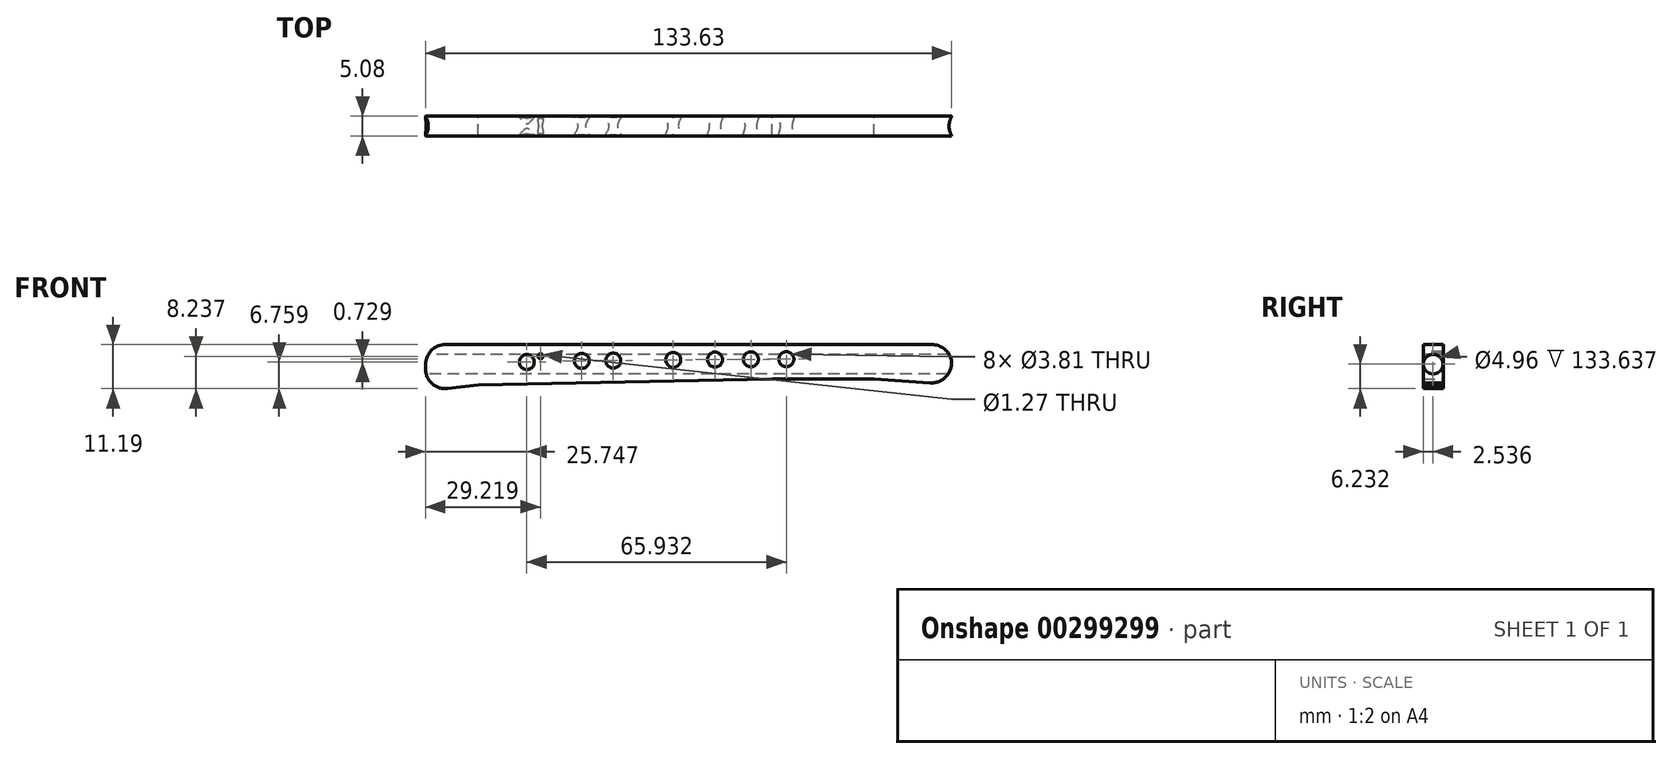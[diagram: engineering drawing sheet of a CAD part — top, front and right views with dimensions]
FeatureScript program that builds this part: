
annotation { "Feature Type Name" : "Feature", "Feature Type Description" : "" }
export const myFeature = defineFeature(function(context is Context, id is Id, definition is map)
    precondition{}
    {
        {
            var Q0;
            Q0=qCreatedBy(makeId("Front.planeOp"),FACE);
            var sketch = newSketch(context, id + "F0", { "sketchPlane" : qUnion([Q0])});
            skLineSegment(sketch, "E0", {"start": v(-67.8, 14.78) * mm, "end": v(-67.8, 2.96) * mm});
            skLineSegment(sketch, "E1", {"start": v(-67.8, 14.78) * mm, "end": v(64.84, 14.78) * mm});
            skLineSegment(sketch, "E2", {"start": v(-67.8, 2.96) * mm, "end": v(-54.4, 4.53) * mm});
            skLineSegment(sketch, "E3", {"start": v(-54.4, 4.53) * mm, "end": v(20.3, 6.1) * mm});
            skLineSegment(sketch, "E4", {"start": v(20.3, 6.1) * mm, "end": v(46.11, 6.1) * mm});
            skLineSegment(sketch, "E5", {"start": v(46.11, 6.1) * mm, "end": v(67.4, 4.53) * mm});
            skLineSegment(sketch, "E6", {"start": v(64.84, 14.78) * mm, "end": v(67.4, 4.53) * mm});
            skSolve(sketch);
        }
        {
            var Q0;
            Q0=makeQuery(id+"F0.imprint","IMPRINT",FACE,{"disambiguationData":[TD([[makeQuery(id+"F0.imprint","IMPRINT",EDGE,{"derivedFrom":sQuery(id+"F0.wireOp",EDGE,"E0")}),1.0]])]});
            extrude(context, id + "F1", {"entities" : qUnion([Q0]), "depth" : 5.08 * mm});
        }
        {
            var Q0;
            Q0=makeQuery(id+"F1.opExtrude","CAP_FACE",FACE,{"disambiguationData":[OSD([sQuery(id+"F0.wireOp",EDGE,"E0"),sQuery(id+"F0.wireOp",EDGE,"E1"),sQuery(id+"F0.wireOp",EDGE,"E2"),sQuery(id+"F0.wireOp",EDGE,"E3"),sQuery(id+"F0.wireOp",EDGE,"E4"),sQuery(id+"F0.wireOp",EDGE,"E5"),sQuery(id+"F0.wireOp",EDGE,"E6")])],"isStart":false});
            var sketch = newSketch(context, id + "F2", { "sketchPlane" : qUnion([Q0])});
            skCircle(sketch, "E7", {"center": v(-42.04, 10.35) * mm, "radius": 1.9 * mm});
            skCircle(sketch, "E8", {"center": v(-38.57, 11.83) * mm, "radius": 0.64 * mm});
            skCircle(sketch, "E9", {"center": v(-28.07, 10.65) * mm, "radius": 1.9 * mm});
            skCircle(sketch, "E10", {"center": v(-20.08, 10.72) * mm, "radius": 1.9 * mm});
            skCircle(sketch, "E11", {"center": v(-4.85, 10.9) * mm, "radius": 1.9 * mm});
            skCircle(sketch, "E12", {"center": v(5.77, 10.98) * mm, "radius": 1.9 * mm});
            skCircle(sketch, "E13", {"center": v(14.9, 11.04) * mm, "radius": 1.9 * mm});
            skCircle(sketch, "E14", {"center": v(23.89, 11.08) * mm, "radius": 1.9 * mm});
            skSolve(sketch);
        }
        {
            var Q0;
            Q0=makeQuery(id+"F2.imprint","IMPRINT",FACE,{"disambiguationData":[TD([[makeQuery(id+"F2.imprint","IMPRINT",EDGE,{"derivedFrom":sQuery(id+"F2.wireOp",EDGE,"E7")}),1.0]])]});
            var Q1;
            Q1=makeQuery(id+"F2.imprint","IMPRINT",FACE,{"disambiguationData":[TD([[makeQuery(id+"F2.imprint","IMPRINT",EDGE,{"derivedFrom":sQuery(id+"F2.wireOp",EDGE,"E9")}),1.0]])]});
            var Q2;
            Q2=makeQuery(id+"F2.imprint","IMPRINT",FACE,{"disambiguationData":[TD([[makeQuery(id+"F2.imprint","IMPRINT",EDGE,{"derivedFrom":sQuery(id+"F2.wireOp",EDGE,"E10")}),1.0]])]});
            var Q3;
            Q3=makeQuery(id+"F2.imprint","IMPRINT",FACE,{"disambiguationData":[TD([[makeQuery(id+"F2.imprint","IMPRINT",EDGE,{"derivedFrom":sQuery(id+"F2.wireOp",EDGE,"E12")}),1.0]])]});
            var Q4;
            Q4=makeQuery(id+"F2.imprint","IMPRINT",FACE,{"disambiguationData":[TD([[makeQuery(id+"F2.imprint","IMPRINT",EDGE,{"derivedFrom":sQuery(id+"F2.wireOp",EDGE,"E11")}),1.0]])]});
            var Q5;
            Q5=makeQuery(id+"F2.imprint","IMPRINT",FACE,{"disambiguationData":[TD([[makeQuery(id+"F2.imprint","IMPRINT",EDGE,{"derivedFrom":sQuery(id+"F2.wireOp",EDGE,"E13")}),1.0]])]});
            var Q6;
            Q6=makeQuery(id+"F2.imprint","IMPRINT",FACE,{"disambiguationData":[TD([[makeQuery(id+"F2.imprint","IMPRINT",EDGE,{"derivedFrom":sQuery(id+"F2.wireOp",EDGE,"E14")}),1.0]])]});
            var Q7;
            Q7=makeQuery(id+"F2.imprint","IMPRINT",FACE,{"disambiguationData":[TD([[makeQuery(id+"F2.imprint","IMPRINT",EDGE,{"derivedFrom":sQuery(id+"F2.wireOp",EDGE,"E8")}),1.0]])]});
            extrude(context, id + "F3", {"entities" : qUnion([Q0, Q1, Q2, Q3, Q4, Q5, Q6, Q7]), "operationType" : NewBodyOperationType.REMOVE, "endBound" : BoundingType.THROUGH_ALL, "oppositeDirection" : true, "depth" : 25.4 * mm});
        }
        {
            var Q0;
            Q0=makeQuery(id+"F1.opExtrude","SWEPT_FACE",FACE,{"disambiguationData":[OSD([sQuery(id+"F0.wireOp",EDGE,"E0")])]});
            var sketch = newSketch(context, id + "F4", { "sketchPlane" : qUnion([Q0])});
            skLineSegment(sketch, "E15", {"start": v(0, 14.78) * mm, "end": v(5.08, 14.78) * mm});
            skLineSegment(sketch, "E16", {"start": v(5.08, 14.78) * mm, "end": v(5.08, 2.96) * mm});
            skLineSegment(sketch, "E17", {"start": v(5.08, 2.96) * mm, "end": v(0, 2.96) * mm});
            skLineSegment(sketch, "E18", {"start": v(0, 2.96) * mm, "end": v(0, 14.78) * mm});
            skSolve(sketch);
        }
        {
            var Q0;
            Q0=makeQuery(id+"F4.imprint","IMPRINT",FACE,{"disambiguationData":[TD([[makeQuery(id+"F4.imprint","IMPRINT",EDGE,{"derivedFrom":sQuery(id+"F4.wireOp",EDGE,"E15")}),1.0]])]});
            var sketch = newSketch(context, id + "F5", { "sketchPlane" : qUnion([Q0])});
            skCircle(sketch, "E19", {"center": v(2.54, 9.82) * mm, "radius": 2.48 * mm});
            skSolve(sketch);
        }
        {
            var Q0;
            Q0 = qSketchRegion(id + "F5", true);
            extrude(context, id + "F6", {"entities" : qUnion([Q0]), "operationType" : NewBodyOperationType.REMOVE, "endBound" : BoundingType.THROUGH_ALL, "oppositeDirection" : true, "depth" : 25.4 * mm});
        }
        {
            var Q0;
            Q0=makeQuery(id+"F1.opExtrude","SWEPT_EDGE",EDGE,{"disambiguationData":[OSD([sQuery(id+"F0.wireOp",EDGE,"E0"),sQuery(id+"F0.wireOp",EDGE,"E1")])]});
            var Q1;
            Q1=makeQuery(id+"F1.opExtrude","SWEPT_EDGE",EDGE,{"disambiguationData":[OSD([sQuery(id+"F0.wireOp",EDGE,"E0"),sQuery(id+"F0.wireOp",EDGE,"E2")])]});
            fillet(context, id + "F7", {"entities" : qUnion([Q0, Q1]), "radius" : 5.08 * mm, "tangentPropagation" : true, "allowEdgeOverflow" : false});
        }
        {
            var Q0;
            Q0=makeQuery(id+"F1.opExtrude","SWEPT_EDGE",EDGE,{"disambiguationData":[OSD([sQuery(id+"F0.wireOp",EDGE,"E1"),sQuery(id+"F0.wireOp",EDGE,"E6")])]});
            var Q1;
            Q1=makeQuery(id+"F1.opExtrude","SWEPT_EDGE",EDGE,{"disambiguationData":[OSD([sQuery(id+"F0.wireOp",EDGE,"E5"),sQuery(id+"F0.wireOp",EDGE,"E6")])]});
            fillet(context, id + "F8", {"entities" : qUnion([Q0, Q1]), "radius" : 5.08 * mm, "tangentPropagation" : true, "allowEdgeOverflow" : false});
        }
    });
